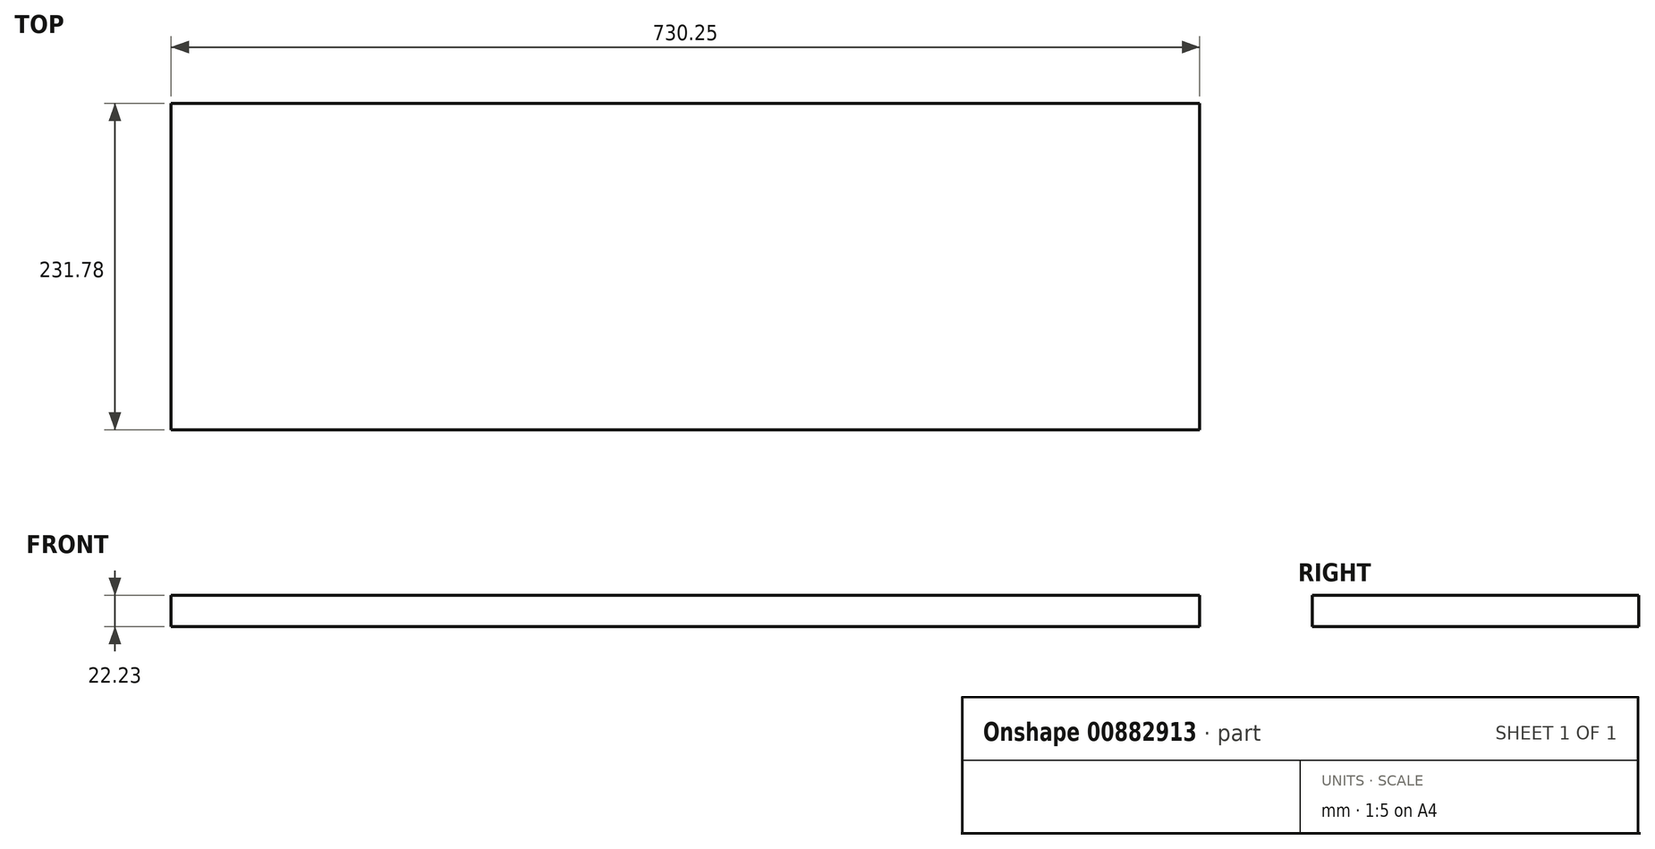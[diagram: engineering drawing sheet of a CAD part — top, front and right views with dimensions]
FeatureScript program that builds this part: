
annotation { "Feature Type Name" : "Feature", "Feature Type Description" : "" }
export const myFeature = defineFeature(function(context is Context, id is Id, definition is map)
    precondition{}
    {
        {
            var Q0;
            Q0=qCreatedBy(makeId("Right.planeOp"),FACE);
            var sketch = newSketch(context, id + "F0", { "sketchPlane" : qUnion([Q0])});
            skLineSegment(sketch, "E0.bottom", {"start": v(0, 0) * mm, "end": v(231.77, 0) * mm});
            skLineSegment(sketch, "E0.top", {"start": v(0, -22.22) * mm, "end": v(231.78, -22.22) * mm});
            skLineSegment(sketch, "E0.left", {"start": v(0, 0) * mm, "end": v(0, -22.22) * mm});
            skLineSegment(sketch, "E0.right", {"start": v(231.78, 0) * mm, "end": v(231.78, -22.22) * mm});
            skSolve(sketch);
        }
        {
            var Q0;
            Q0=makeQuery(id+"F0.imprint","IMPRINT",FACE,{"disambiguationData":[TD([[makeQuery(id+"F0.imprint","IMPRINT",EDGE,{"derivedFrom":sQuery(id+"F0.wireOp",EDGE,"E0.bottom")}),-1.0]])]});
            extrude(context, id + "F1", {"entities" : qUnion([Q0]), "depth" : 730.25 * mm, "offsetDistance" : 25.4 * mm});
        }
    });
